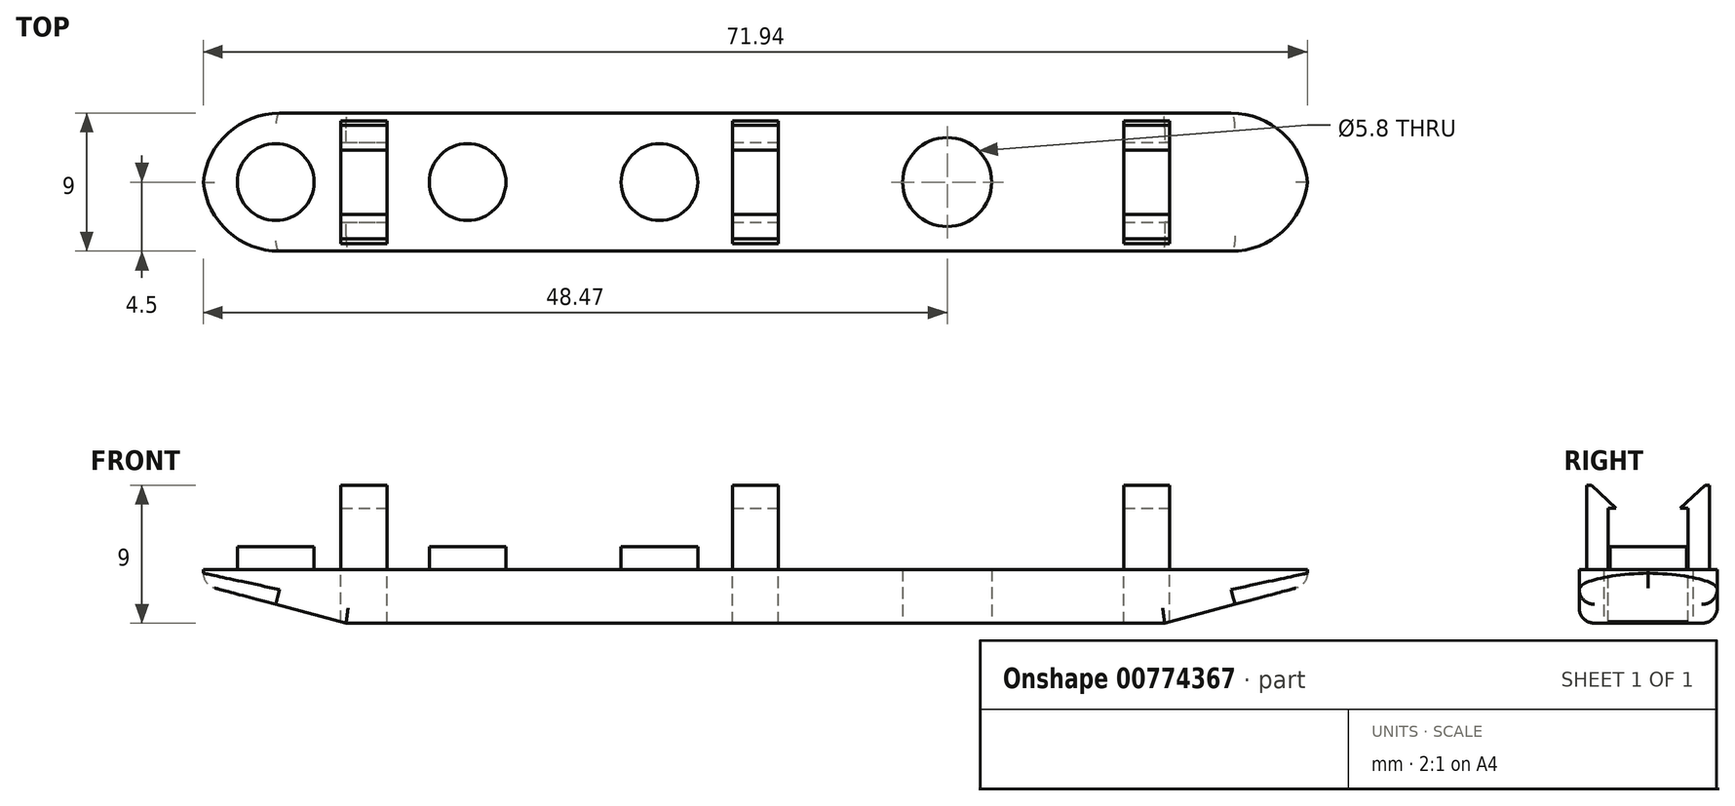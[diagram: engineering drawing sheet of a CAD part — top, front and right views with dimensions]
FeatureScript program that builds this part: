
annotation { "Feature Type Name" : "Feature", "Feature Type Description" : "" }
export const myFeature = defineFeature(function(context is Context, id is Id, definition is map)
    precondition{}
    {
        {
            var Q0;
            Q0=qCreatedBy(makeId("Front.planeOp"),FACE);
            var sketch = newSketch(context, id + "F0", { "sketchPlane" : qUnion([Q0])});
            skLineSegment(sketch, "E0.bottom", {"start": v(-36, 9) * mm, "end": v(36, 9) * mm});
            skLineSegment(sketch, "E0.top", {"start": v(-36, 0) * mm, "end": v(36, 0) * mm});
            skLineSegment(sketch, "E0.left", {"start": v(-36, 9) * mm, "end": v(-36, 0) * mm});
            skLineSegment(sketch, "E0.right", {"start": v(36, 9) * mm, "end": v(36, 0) * mm});
            skSolve(sketch);
        }
        {
            var Q0;
            Q0=makeQuery(id+"F0.imprint","IMPRINT",FACE,{"disambiguationData":[TD([[makeQuery(id+"F0.imprint","IMPRINT",EDGE,{"derivedFrom":sQuery(id+"F0.wireOp",EDGE,"E0.bottom")}),-1.0]])]});
            extrude(context, id + "F1", {"entities" : qUnion([Q0]), "depth" : 9 * mm, "offsetDistance" : 25 * mm});
        }
        {
            var Q0;
            Q0=makeQuery(id+"F1.opExtrude","SWEPT_FACE",FACE,{"disambiguationData":[OSD([sQuery(id+"F0.wireOp",EDGE,"E0.right")])]});
            var sketch = newSketch(context, id + "F2", { "sketchPlane" : qUnion([Q0])});
            skLineSegment(sketch, "E1", {"start": v(-8.2, 9) * mm, "end": v(-6.6, 7.5) * mm});
            skLineSegment(sketch, "E2", {"start": v(-6.6, 7.5) * mm, "end": v(-7.1, 7.5) * mm});
            skLineSegment(sketch, "E3", {"start": v(-7.1, 7.5) * mm, "end": v(-7.1, 5) * mm});
            skLineSegment(sketch, "E4", {"start": v(-7.1, 5) * mm, "end": v(-1.9, 5) * mm});
            skLineSegment(sketch, "E5", {"start": v(-1.9, 5) * mm, "end": v(-1.9, 7.5) * mm});
            skLineSegment(sketch, "E6", {"start": v(-1.9, 7.5) * mm, "end": v(-2.4, 7.5) * mm});
            skLineSegment(sketch, "E7", {"start": v(-2.4, 7.5) * mm, "end": v(-0.8, 9) * mm});
            skLineSegment(sketch, "E8", {"start": v(-0.8, 9) * mm, "end": v(-0.8, 9) * mm});
            skLineSegment(sketch, "E9", {"start": v(-0.8, 9) * mm, "end": v(-0.5, 9) * mm});
            skLineSegment(sketch, "E10", {"start": v(-0.5, 9) * mm, "end": v(-0.5, 5) * mm});
            skLineSegment(sketch, "E11", {"start": v(-0.5, 5) * mm, "end": v(0, 5) * mm});
            skLineSegment(sketch, "E12", {"start": v(0, 5) * mm, "end": v(0, 9) * mm});
            skLineSegment(sketch, "E13", {"start": v(-9, 9) * mm, "end": v(-9, 5) * mm});
            skLineSegment(sketch, "E14", {"start": v(-9, 5) * mm, "end": v(-8.5, 5) * mm});
            skLineSegment(sketch, "E15", {"start": v(-8.5, 5) * mm, "end": v(-8.5, 9) * mm});
            skLineSegment(sketch, "E16", {"start": v(-8.5, 9) * mm, "end": v(-8.2, 9) * mm});
            skLineSegment(sketch, "E17", {"start": v(-8.2, 9) * mm, "end": v(-8.2, 9) * mm});
            skLineSegment(sketch, "E18", {"start": v(-8.2, 9) * mm, "end": v(-0.8, 9) * mm});
            skLineSegment(sketch, "E19", {"start": v(-9, 9) * mm, "end": v(-8.5, 9) * mm});
            skLineSegment(sketch, "E20", {"start": v(-0.5, 9) * mm, "end": v(0, 9) * mm});
            skSolve(sketch);
        }
        {
            var Q0;
            Q0=makeQuery(id+"F2.imprint","IMPRINT",FACE,{"disambiguationData":[TD([[makeQuery(id+"F2.imprint","IMPRINT",EDGE,{"derivedFrom":sQuery(id+"F2.wireOp",EDGE,"E1")}),1.0]])]});
            var Q1;
            {var subQ6=sQuery(id+"F2.wireOp",EDGE,"E8");Q1=makeQuery(id+"F2.imprint","IMPRINT",FACE,{"disambiguationData":[TD([[makeQuery(id+"F2.imprint","IMPRINT",EDGE,{"derivedFrom":subQ6}),1.0]])]});}
            var Q2;
            Q2=makeQuery(id+"F2.imprint","IMPRINT",FACE,{"disambiguationData":[TD([[makeQuery(id+"F2.imprint","IMPRINT",EDGE,{"derivedFrom":sQuery(id+"F2.wireOp",EDGE,"E13")}),1.0]])]});
            var Q3;
            Q3=makeQuery(id+"F2.imprint","IMPRINT",FACE,{"disambiguationData":[TD([[makeQuery(id+"F2.imprint","IMPRINT",EDGE,{"derivedFrom":sQuery(id+"F2.wireOp",EDGE,"E10")}),1.0]])]});
            extrude(context, id + "F3", {"entities" : qUnion([Q0, Q1, Q2, Q3]), "operationType" : NewBodyOperationType.REMOVE, "endBound" : BoundingType.THROUGH_ALL, "oppositeDirection" : true, "depth" : 25 * mm, "offsetDistance" : 25 * mm});
        }
        {
            var Q0;
            Q0=makeQuery(id+"F1.opExtrude","CAP_FACE",FACE,{"disambiguationData":[OSD([sQuery(id+"F0.wireOp",EDGE,"E0.bottom"),sQuery(id+"F0.wireOp",EDGE,"E0.top"),sQuery(id+"F0.wireOp",EDGE,"E0.left"),sQuery(id+"F0.wireOp",EDGE,"E0.right")])],"isStart":false});
            var sketch = newSketch(context, id + "F4", { "sketchPlane" : qUnion([Q0])});
            skLineSegment(sketch, "E21.bottom", {"start": v(1.5, 9) * mm, "end": v(24, 9) * mm});
            skLineSegment(sketch, "E21.top", {"start": v(1.5, 5) * mm, "end": v(24, 5) * mm});
            skLineSegment(sketch, "E21.left", {"start": v(1.5, 9) * mm, "end": v(1.5, 5) * mm});
            skLineSegment(sketch, "E21.right", {"start": v(24, 9) * mm, "end": v(24, 5) * mm});
            skLineSegment(sketch, "E22.bottom", {"start": v(-1.5, 9) * mm, "end": v(-24, 9) * mm});
            skLineSegment(sketch, "E22.top", {"start": v(-1.5, 5) * mm, "end": v(-24, 5) * mm});
            skLineSegment(sketch, "E22.left", {"start": v(-1.5, 9) * mm, "end": v(-1.5, 5) * mm});
            skLineSegment(sketch, "E22.right", {"start": v(-24, 9) * mm, "end": v(-24, 5) * mm});
            skLineSegment(sketch, "E23.bottom", {"start": v(27, 9) * mm, "end": v(36, 9) * mm});
            skLineSegment(sketch, "E23.top", {"start": v(27, 5) * mm, "end": v(36, 5) * mm});
            skLineSegment(sketch, "E23.left", {"start": v(27, 9) * mm, "end": v(27, 5) * mm});
            skLineSegment(sketch, "E23.right", {"start": v(36, 9) * mm, "end": v(36, 5) * mm});
            skLineSegment(sketch, "E24.bottom", {"start": v(-27, 9) * mm, "end": v(-36, 9) * mm});
            skLineSegment(sketch, "E24.top", {"start": v(-27, 5) * mm, "end": v(-36, 5) * mm});
            skLineSegment(sketch, "E24.left", {"start": v(-27, 9) * mm, "end": v(-27, 5) * mm});
            skLineSegment(sketch, "E24.right", {"start": v(-36, 9) * mm, "end": v(-36, 5) * mm});
            skSolve(sketch);
        }
        {
            var Q0;
            Q0=makeQuery(id+"F4.imprint","IMPRINT",FACE,{"disambiguationData":[TD([[makeQuery(id+"F4.imprint","IMPRINT",EDGE,{"derivedFrom":sQuery(id+"F4.wireOp",EDGE,"E23.bottom")}),-1.0]])]});
            var Q1;
            Q1=makeQuery(id+"F4.imprint","IMPRINT",FACE,{"disambiguationData":[TD([[makeQuery(id+"F4.imprint","IMPRINT",EDGE,{"derivedFrom":sQuery(id+"F4.wireOp",EDGE,"E24.bottom")}),-1.0]])]});
            var Q2;
            Q2=makeQuery(id+"F4.imprint","IMPRINT",FACE,{"disambiguationData":[TD([[makeQuery(id+"F4.imprint","IMPRINT",EDGE,{"derivedFrom":sQuery(id+"F4.wireOp",EDGE,"E22.bottom")}),-1.0]])]});
            var Q3;
            Q3=makeQuery(id+"F4.imprint","IMPRINT",FACE,{"disambiguationData":[TD([[makeQuery(id+"F4.imprint","IMPRINT",EDGE,{"derivedFrom":sQuery(id+"F4.wireOp",EDGE,"E21.bottom")}),-1.0]])]});
            var Q4;
            Q4=makeQuery(id+"F4.imprint","IMPRINT",FACE,{"disambiguationData":[TD([[makeQuery(id+"F4.imprint","IMPRINT",EDGE,{"derivedFrom":sQuery(id+"F4.wireOp",EDGE,"E22.bottom")}),1.0]])]});
            var Q5;
            Q5=makeQuery(id+"F4.imprint","IMPRINT",FACE,{"disambiguationData":[TD([[makeQuery(id+"F4.imprint","IMPRINT",EDGE,{"derivedFrom":sQuery(id+"F4.wireOp",EDGE,"E24.bottom")}),1.0]])]});
            extrude(context, id + "F5", {"entities" : qUnion([Q0, Q1, Q2, Q3, Q4, Q5]), "operationType" : NewBodyOperationType.REMOVE, "endBound" : BoundingType.THROUGH_ALL, "oppositeDirection" : true, "depth" : 25 * mm, "offsetDistance" : 25 * mm});
        }
        {
            var Q0;
            Q0=makeQuery(id+"F1.opExtrude","SWEPT_EDGE",EDGE,{"disambiguationData":[OSD([sQuery(id+"F0.wireOp",EDGE,"E0.top"),sQuery(id+"F0.wireOp",EDGE,"E0.right")])]});
            var Q1;
            Q1=makeQuery(id+"F1.opExtrude","SWEPT_EDGE",EDGE,{"disambiguationData":[OSD([sQuery(id+"F0.wireOp",EDGE,"E0.top"),sQuery(id+"F0.wireOp",EDGE,"E0.left")])]});
            chamfer(context, id + "F6", {"entities" : qUnion([Q0, Q1]), "chamferType" : ChamferType.OFFSET_ANGLE, "width" : 2.5 * mm, "oppositeDirection" : false, "angle" : 75 * degree, "tangentPropagation" : true});
        }
        {
            var Q0;
            Q0=makeQuery(id+"F1.opExtrude","CAP_EDGE",EDGE,{"disambiguationData":[OSD([sQuery(id+"F0.wireOp",EDGE,"E0.left")])],"isStart":true});
            var Q1;
            Q1=makeQuery(id+"F1.opExtrude","CAP_EDGE",EDGE,{"disambiguationData":[OSD([sQuery(id+"F0.wireOp",EDGE,"E0.left")])],"isStart":false});
            var Q2;
            Q2=makeQuery(id+"F1.opExtrude","CAP_EDGE",EDGE,{"disambiguationData":[OSD([sQuery(id+"F0.wireOp",EDGE,"E0.right")])],"isStart":true});
            var Q3;
            Q3=makeQuery(id+"F1.opExtrude","CAP_EDGE",EDGE,{"disambiguationData":[OSD([sQuery(id+"F0.wireOp",EDGE,"E0.right")])],"isStart":false});
            fillet(context, id + "F7", {"entities" : qUnion([Q0, Q1, Q2, Q3]), "radius" : 5 * mm, "tangentPropagation" : true, "allowEdgeOverflow" : false});
        }
        {
            var Q0;
            Q0=makeQuery(id+"F1.opExtrude","CAP_EDGE",EDGE,{"disambiguationData":[OSD([sQuery(id+"F0.wireOp",EDGE,"E0.top")])],"isStart":true});
            var Q1;
            Q1=makeQuery(id+"F1.opExtrude","CAP_EDGE",EDGE,{"disambiguationData":[OSD([sQuery(id+"F0.wireOp",EDGE,"E0.top")])],"isStart":false});
            var Q2;
            {var subQ0=sQuery(id+"F0.wireOp",EDGE,"E0.right");Q2=makeQuery(id+"F7.opFillet","BLEND_EDGE",EDGE,{"blendedFrom":[makeQuery(id+"F1.opExtrude","CAP_EDGE",EDGE,{"disambiguationData":[OSD([subQ0])],"isStart":true}),makeQuery(id+"F6.opChamfer","BLEND_FACE",FACE,{"disambiguationData":[OSD([sQuery(id+"F0.wireOp",EDGE,"E0.top"),subQ0])]})],"blendedInto":[makeQuery(id+"F6.opChamfer","BLEND_FACE",FACE,{"disambiguationData":[OSD([sQuery(id+"F0.wireOp",EDGE,"E0.top"),subQ0])]})]});}
            var Q3;
            {var subQ0=sQuery(id+"F0.wireOp",EDGE,"E0.right");Q3=makeQuery(id+"F7.opFillet","BLEND_EDGE",EDGE,{"blendedFrom":[makeQuery(id+"F1.opExtrude","CAP_EDGE",EDGE,{"disambiguationData":[OSD([subQ0])],"isStart":false}),makeQuery(id+"F6.opChamfer","BLEND_FACE",FACE,{"disambiguationData":[OSD([sQuery(id+"F0.wireOp",EDGE,"E0.top"),subQ0])]})],"blendedInto":[makeQuery(id+"F6.opChamfer","BLEND_FACE",FACE,{"disambiguationData":[OSD([sQuery(id+"F0.wireOp",EDGE,"E0.top"),subQ0])]})]});}
            var Q4;
            {var subQ0=sQuery(id+"F0.wireOp",EDGE,"E0.left");Q4=makeQuery(id+"F7.opFillet","BLEND_EDGE",EDGE,{"blendedFrom":[makeQuery(id+"F1.opExtrude","CAP_EDGE",EDGE,{"disambiguationData":[OSD([subQ0])],"isStart":true}),makeQuery(id+"F6.opChamfer","BLEND_FACE",FACE,{"disambiguationData":[OSD([sQuery(id+"F0.wireOp",EDGE,"E0.top"),subQ0])]})],"blendedInto":[makeQuery(id+"F6.opChamfer","BLEND_FACE",FACE,{"disambiguationData":[OSD([sQuery(id+"F0.wireOp",EDGE,"E0.top"),subQ0])]})]});}
            var Q5;
            {var subQ0=sQuery(id+"F0.wireOp",EDGE,"E0.left");Q5=makeQuery(id+"F7.opFillet","BLEND_EDGE",EDGE,{"blendedFrom":[makeQuery(id+"F1.opExtrude","CAP_EDGE",EDGE,{"disambiguationData":[OSD([subQ0])],"isStart":false}),makeQuery(id+"F6.opChamfer","BLEND_FACE",FACE,{"disambiguationData":[OSD([sQuery(id+"F0.wireOp",EDGE,"E0.top"),subQ0])]})],"blendedInto":[makeQuery(id+"F6.opChamfer","BLEND_FACE",FACE,{"disambiguationData":[OSD([sQuery(id+"F0.wireOp",EDGE,"E0.top"),subQ0])]})]});}
            fillet(context, id + "F8", {"entities" : qUnion([Q0, Q1, Q2, Q3, Q4, Q5]), "radius" : 1 * mm, "tangentPropagation" : true, "allowEdgeOverflow" : false});
        }
        {
            var Q0;
            Q0=makeQuery(id+"F5.boolean.opBoolean","MERGE",FACE,{"derivedFrom":[makeQuery(id+"F3.boolean.opBoolean","COPY",FACE,{"derivedFrom":makeQuery(id+"F3.opExtrude","SWEPT_FACE",FACE,{"disambiguationData":[OSD([sQuery(id+"F2.wireOp",EDGE,"E4")])]})}),makeQuery(id+"F5.opExtrude","SWEPT_FACE",FACE,{"disambiguationData":[OSD([sQuery(id+"F4.wireOp",EDGE,"E21.top")])]}),makeQuery(id+"F5.opExtrude","SWEPT_FACE",FACE,{"disambiguationData":[OSD([sQuery(id+"F4.wireOp",EDGE,"E22.top")])]}),makeQuery(id+"F5.opExtrude","SWEPT_FACE",FACE,{"disambiguationData":[OSD([sQuery(id+"F4.wireOp",EDGE,"E23.top")])]}),makeQuery(id+"F5.opExtrude","SWEPT_FACE",FACE,{"disambiguationData":[OSD([sQuery(id+"F4.wireOp",EDGE,"E24.top")])]})]});
            var sketch = newSketch(context, id + "F9", { "sketchPlane" : qUnion([Q0])});
            skLineSegment(sketch, "E25", {"start": v(-52.66, -4.5) * mm, "end": v(25.83, -4.5) * mm, "construction": true});
            skCircle(sketch, "E26", {"center": v(6.25, -4.5) * mm, "radius": 2.5 * mm});
            skCircle(sketch, "E27.1.0.0", {"center": v(18.75, -4.5) * mm, "radius": 2.5 * mm});
            skLineSegment(sketch, "E27.1.0.1", {"start": v(-40.16, -4.5) * mm, "end": v(38.33, -4.5) * mm, "construction": true});
            skCircle(sketch, "E27.2.0.0", {"center": v(31.25, -4.5) * mm, "radius": 2.5 * mm});
            skLineSegment(sketch, "E27.2.0.1", {"start": v(-27.66, -4.5) * mm, "end": v(50.83, -4.5) * mm, "construction": true});
            skLineSegment(sketch, "E27.direction1", {"start": v(6.25, -4.5) * mm, "end": v(18.75, -4.5) * mm, "construction": true});
            skCircle(sketch, "E28.MirrorC", {"center": v(-6.25, -4.5) * mm, "radius": 2.5 * mm});
            skCircle(sketch, "E29.MirrorC", {"center": v(-18.75, -4.5) * mm, "radius": 2.5 * mm});
            skCircle(sketch, "E30.MirrorC", {"center": v(-31.25, -4.5) * mm, "radius": 2.5 * mm});
            skSolve(sketch);
        }
        {
            var Q0;
            Q0=makeQuery(id+"F9.imprint","IMPRINT",FACE,{"disambiguationData":[TD([[makeQuery(id+"F9.imprint","IMPRINT",EDGE,{"derivedFrom":sQuery(id+"F9.wireOp",EDGE,"E27.2.0.0")}),1.0]])]});
            var Q1;
            Q1=makeQuery(id+"F9.imprint","IMPRINT",FACE,{"disambiguationData":[TD([[makeQuery(id+"F9.imprint","IMPRINT",EDGE,{"derivedFrom":sQuery(id+"F9.wireOp",EDGE,"E27.1.0.0")}),1.0]])]});
            var Q2;
            Q2=makeQuery(id+"F9.imprint","IMPRINT",FACE,{"disambiguationData":[TD([[makeQuery(id+"F9.imprint","IMPRINT",EDGE,{"derivedFrom":sQuery(id+"F9.wireOp",EDGE,"E26")}),1.0]])]});
            var Q3;
            Q3=makeQuery(id+"F9.imprint","IMPRINT",FACE,{"disambiguationData":[TD([[makeQuery(id+"F9.imprint","IMPRINT",EDGE,{"derivedFrom":sQuery(id+"F9.wireOp",EDGE,"E28.MirrorC")}),-1.0]])]});
            var Q4;
            Q4=makeQuery(id+"F9.imprint","IMPRINT",FACE,{"disambiguationData":[TD([[makeQuery(id+"F9.imprint","IMPRINT",EDGE,{"derivedFrom":sQuery(id+"F9.wireOp",EDGE,"E29.MirrorC")}),-1.0]])]});
            var Q5;
            Q5=makeQuery(id+"F9.imprint","IMPRINT",FACE,{"disambiguationData":[TD([[makeQuery(id+"F9.imprint","IMPRINT",EDGE,{"derivedFrom":sQuery(id+"F9.wireOp",EDGE,"E30.MirrorC")}),-1.0]])]});
            extrude(context, id + "F10", {"entities" : qUnion([Q0, Q1, Q2, Q3, Q4, Q5]), "operationType" : NewBodyOperationType.REMOVE, "oppositeDirection" : true, "depth" : 1.5 * mm, "offsetDistance" : 25 * mm});
        }
        {
            var Q0;
            Q0=makeQuery(id+"F1.opExtrude","SWEPT_FACE",FACE,{"disambiguationData":[OSD([sQuery(id+"F0.wireOp",EDGE,"E0.top")])]});
            var sketch = newSketch(context, id + "F11", { "sketchPlane" : qUnion([Q0])});
            skCircle(sketch, "E31", {"center": v(12.5, 4.5) * mm, "radius": 2.9 * mm});
            skSolve(sketch);
        }
        {
            var Q0;
            Q0=makeQuery(id+"F11.imprint","IMPRINT",FACE,{"disambiguationData":[TD([[makeQuery(id+"F11.imprint","IMPRINT",EDGE,{"derivedFrom":sQuery(id+"F11.wireOp",EDGE,"E31")}),1.0]])]});
            extrude(context, id + "F12", {"entities" : qUnion([Q0]), "operationType" : NewBodyOperationType.REMOVE, "oppositeDirection" : true, "depth" : 3.6 * mm, "offsetDistance" : 25 * mm});
        }
        {
            var Q0;
            Q0=makeQuery(id+"F5.boolean.opBoolean","MERGE",FACE,{"derivedFrom":[makeQuery(id+"F3.boolean.opBoolean","COPY",FACE,{"derivedFrom":makeQuery(id+"F3.opExtrude","SWEPT_FACE",FACE,{"disambiguationData":[OSD([sQuery(id+"F2.wireOp",EDGE,"E4")])]})}),makeQuery(id+"F5.opExtrude","SWEPT_FACE",FACE,{"disambiguationData":[OSD([sQuery(id+"F4.wireOp",EDGE,"E21.top")])]}),makeQuery(id+"F5.opExtrude","SWEPT_FACE",FACE,{"disambiguationData":[OSD([sQuery(id+"F4.wireOp",EDGE,"E22.top")])]}),makeQuery(id+"F5.opExtrude","SWEPT_FACE",FACE,{"disambiguationData":[OSD([sQuery(id+"F4.wireOp",EDGE,"E23.top")])]}),makeQuery(id+"F5.opExtrude","SWEPT_FACE",FACE,{"disambiguationData":[OSD([sQuery(id+"F4.wireOp",EDGE,"E24.top")])]})]});
            var sketch = newSketch(context, id + "F13", { "sketchPlane" : qUnion([Q0])});
            skLineSegment(sketch, "E32.bottom", {"start": v(24, -1.9) * mm, "end": v(27, -1.9) * mm});
            skLineSegment(sketch, "E32.top", {"start": v(24, -7.1) * mm, "end": v(27, -7.1) * mm});
            skLineSegment(sketch, "E32.left", {"start": v(24, -1.9) * mm, "end": v(24, -7.1) * mm});
            skLineSegment(sketch, "E32.right", {"start": v(27, -1.9) * mm, "end": v(27, -7.1) * mm});
            skLineSegment(sketch, "E33.bottom", {"start": v(-1.5, -1.9) * mm, "end": v(1.5, -1.9) * mm});
            skLineSegment(sketch, "E33.top", {"start": v(-1.5, -7.1) * mm, "end": v(1.5, -7.1) * mm});
            skLineSegment(sketch, "E33.left", {"start": v(-1.5, -1.9) * mm, "end": v(-1.5, -7.1) * mm});
            skLineSegment(sketch, "E33.right", {"start": v(1.5, -1.9) * mm, "end": v(1.5, -7.1) * mm});
            skLineSegment(sketch, "E34.bottom", {"start": v(-27, -1.9) * mm, "end": v(-24, -1.9) * mm});
            skLineSegment(sketch, "E34.top", {"start": v(-27, -7.1) * mm, "end": v(-24, -7.1) * mm});
            skLineSegment(sketch, "E34.left", {"start": v(-27, -1.9) * mm, "end": v(-27, -7.1) * mm});
            skLineSegment(sketch, "E34.right", {"start": v(-24, -1.9) * mm, "end": v(-24, -7.1) * mm});
            skSolve(sketch);
        }
        {
            var Q0;
            Q0=makeQuery(id+"F13.imprint","IMPRINT",FACE,{"disambiguationData":[TD([[makeQuery(id+"F13.imprint","IMPRINT",EDGE,{"derivedFrom":sQuery(id+"F13.wireOp",EDGE,"E32.bottom")}),-1.0]])]});
            var Q1;
            Q1=makeQuery(id+"F13.imprint","IMPRINT",FACE,{"disambiguationData":[TD([[makeQuery(id+"F13.imprint","IMPRINT",EDGE,{"derivedFrom":sQuery(id+"F13.wireOp",EDGE,"E33.bottom")}),-1.0]])]});
            var Q2;
            Q2=makeQuery(id+"F13.imprint","IMPRINT",FACE,{"disambiguationData":[TD([[makeQuery(id+"F13.imprint","IMPRINT",EDGE,{"derivedFrom":sQuery(id+"F13.wireOp",EDGE,"E34.bottom")}),-1.0]])]});
            extrude(context, id + "F14", {"entities" : qUnion([Q0, Q1, Q2]), "operationType" : NewBodyOperationType.REMOVE, "endBound" : BoundingType.THROUGH_ALL, "oppositeDirection" : true, "depth" : 25 * mm, "offsetDistance" : 25 * mm});
        }
    });
